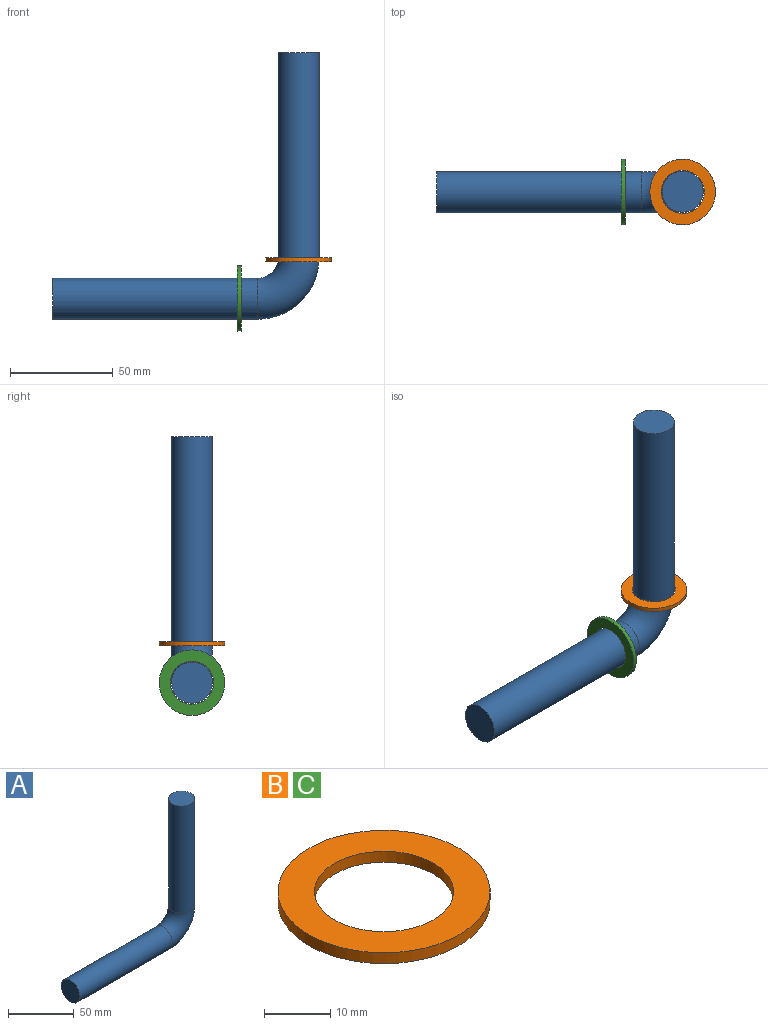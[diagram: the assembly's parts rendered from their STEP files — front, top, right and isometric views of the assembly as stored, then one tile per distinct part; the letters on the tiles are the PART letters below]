
ASSEMBLY  parts=3 mates=2
PART A: 5 faces, bbox 132.5x20x132.5 mm
  f0: cylinder r=10mm len=100mm, axis (-1,0,0), area 6283.2mm2, adj f1,f3
  f1: plane 20x20mm, normal (-1,0,0), area 314.2mm2, adj f0
  f2: plane 20x20mm, normal (0,0,1), area 314.2mm2, adj f4
  f3: torus R=20mm, axis (0,-1,0), area 1973.9mm2, adj f0,f4
  f4: cylinder r=10mm len=100mm, axis (0,0,1), area 6283.2mm2, adj f2,f3
PART B: 4 faces, bbox 32x32x2 mm
  f0: cylinder r=16mm len=32mm, axis (0,0,1), area 201.1mm2, adj f2,f3
  f1: cylinder r=10.5mm len=21mm, axis (0,0,1), area 131.9mm2, adj f2,f3
  f2: plane 32x32mm, normal (0,0,-1), area 457.9mm2, adj f0,f1
  f3: plane 32x32mm, normal (0,0,1), area 457.9mm2, adj f0,f1
PART C: same geometry as B
PLACE A at identity
PLACE B t=(0,0,-23.5)mm
PLACE C rot(axis=(0,-1,0),90deg) t=(133.5,0,-120)mm
MATE fastened C.f0 <-> A.f0  axis (-1,0,0) through (90,0,0)mm
MATE fastened B.f0 <-> A.f4  axis (0,0,1) through (120,0,20)mm
